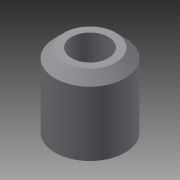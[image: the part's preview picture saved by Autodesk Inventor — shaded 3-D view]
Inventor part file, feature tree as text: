
AUTODESK INVENTOR PART (.ipt)
format: ipt  version: 2015 (Build 190159000, 159)  size: 83,456 bytes
history: native  units: in
note: dims shown in document units (in); Inventor stores cm internally (conversion verified against a paired STEP export)
features: extrude x1, chamfer x1, sketch x1
ambient origin geometry x8: Origin, YZ Plane, XZ Plane, XY Plane, X Axis, Y Axis, Z Axis, Center Point
bodies: Solid1 (feature_tree)
feature tree (3):
  extrude  "Extrusion1"  Depth=0.125in
  chamfer  "Chamfer1"  Distance=0.5in
  sketch  "Sketch1"  dims[d0=0.476in d1=0.25in d2=0.5in d3=0.0in d4=0.0625in d5=0.125in d6=45.0deg]
